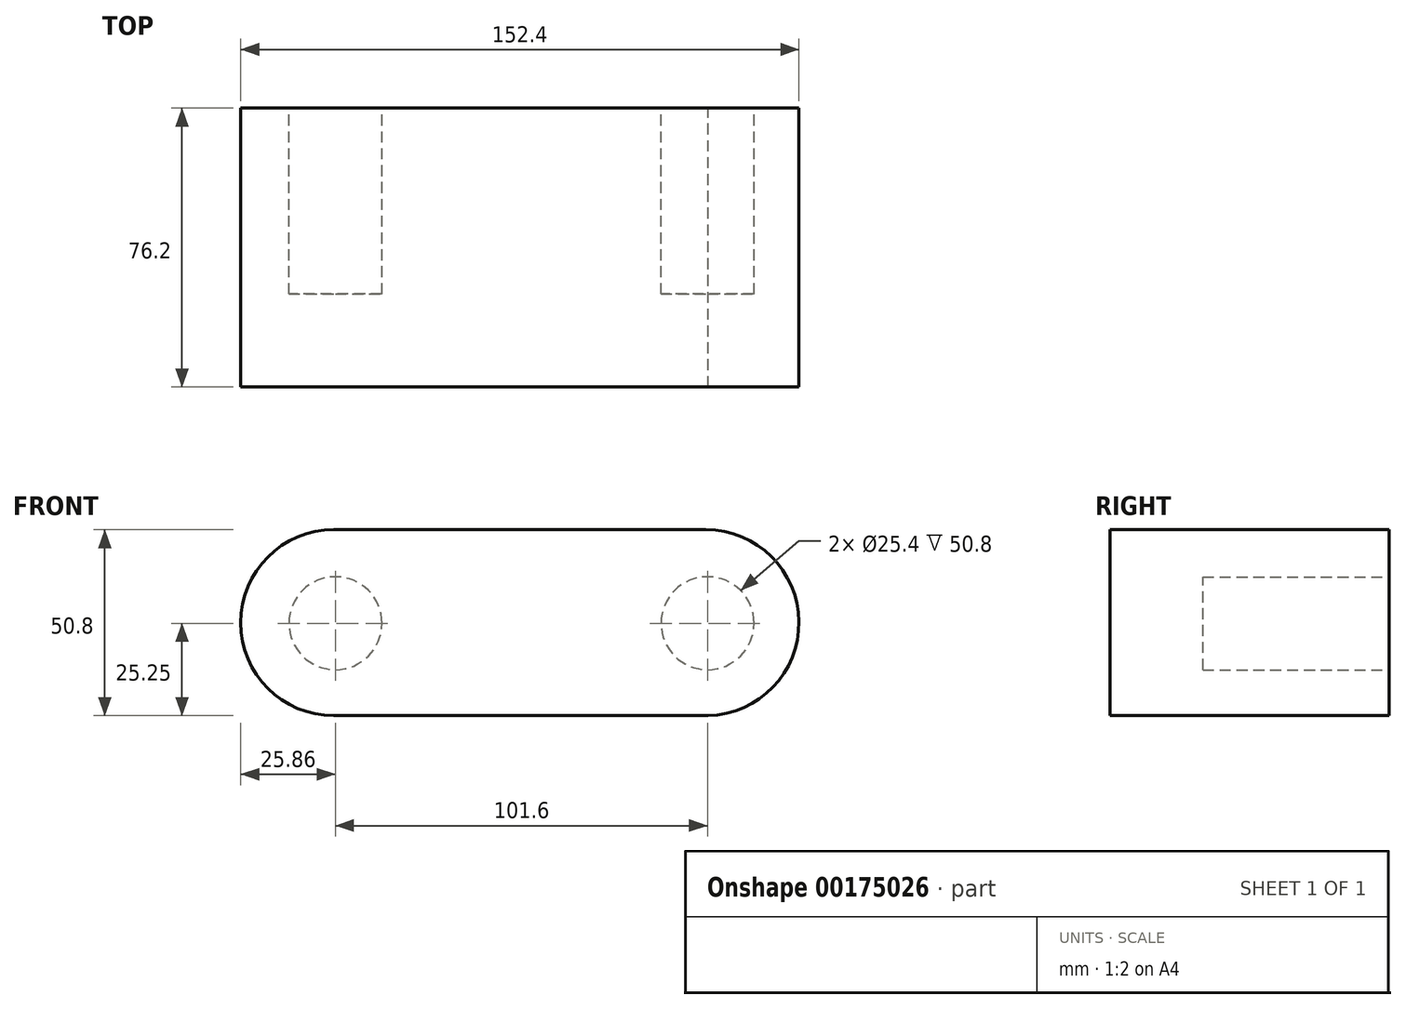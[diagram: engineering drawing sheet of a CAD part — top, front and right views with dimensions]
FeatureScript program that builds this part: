
annotation { "Feature Type Name" : "Feature", "Feature Type Description" : "" }
export const myFeature = defineFeature(function(context is Context, id is Id, definition is map)
    precondition{}
    {
        {
            var Q0;
            Q0=qCreatedBy(makeId("Front.planeOp"),FACE);
            var sketch = newSketch(context, id + "F0", { "sketchPlane" : qUnion([Q0])});
            skLineSegment(sketch, "E0.bottom", {"start": v(-51.26, 25.55) * mm, "end": v(50.34, 25.55) * mm});
            skLineSegment(sketch, "E0.top", {"start": v(-51.26, -25.25) * mm, "end": v(50.94, -25.25) * mm});
            skArc(sketch, "E1", {"start": v(-51.26, 25.55) * mm, "mid": v(-76.66, 0.15) * mm, "end": v(-51.26, -25.25) * mm});
            skArc(sketch, "E2", {"start": v(50.94, -25.25) * mm, "mid": v(75.74, 0.44) * mm, "end": v(50.34, 25.55) * mm});
            skSolve(sketch);
        }
        {
            var Q0;
            Q0 = qSketchRegion(id + "F0", true);
            extrude(context, id + "F1", {"entities" : qUnion([Q0]), "depth" : 76.2 * mm});
        }
        {
            var Q0;
            Q0=qCreatedBy(makeId("Front.planeOp"),FACE);
            var sketch = newSketch(context, id + "F2", { "sketchPlane" : qUnion([Q0])});
            skCircle(sketch, "E3", {"center": v(-50.8, 0) * mm, "radius": 12.7 * mm});
            skCircle(sketch, "E4", {"center": v(50.8, 0) * mm, "radius": 12.7 * mm});
            skSolve(sketch);
        }
        {
            var Q0;
            Q0=makeQuery(id+"F2.imprint","IMPRINT",FACE,{"disambiguationData":[TD([[makeQuery(id+"F2.imprint","IMPRINT",EDGE,{"derivedFrom":sQuery(id+"F2.wireOp",EDGE,"E4")}),1.0]])]});
            var Q1;
            Q1=makeQuery(id+"F2.imprint","IMPRINT",FACE,{"disambiguationData":[TD([[makeQuery(id+"F2.imprint","IMPRINT",EDGE,{"derivedFrom":sQuery(id+"F2.wireOp",EDGE,"E3")}),1.0]])]});
            var Q2;
            Q2=sQuery(id+"F2.wireOp",EDGE,"E3");
            extrude(context, id + "F3", {"entities" : qUnion([Q0, Q1]), "operationType" : NewBodyOperationType.REMOVE, "surfaceEntities" : qUnion([Q2]), "depth" : 50.8 * mm});
        }
    });
